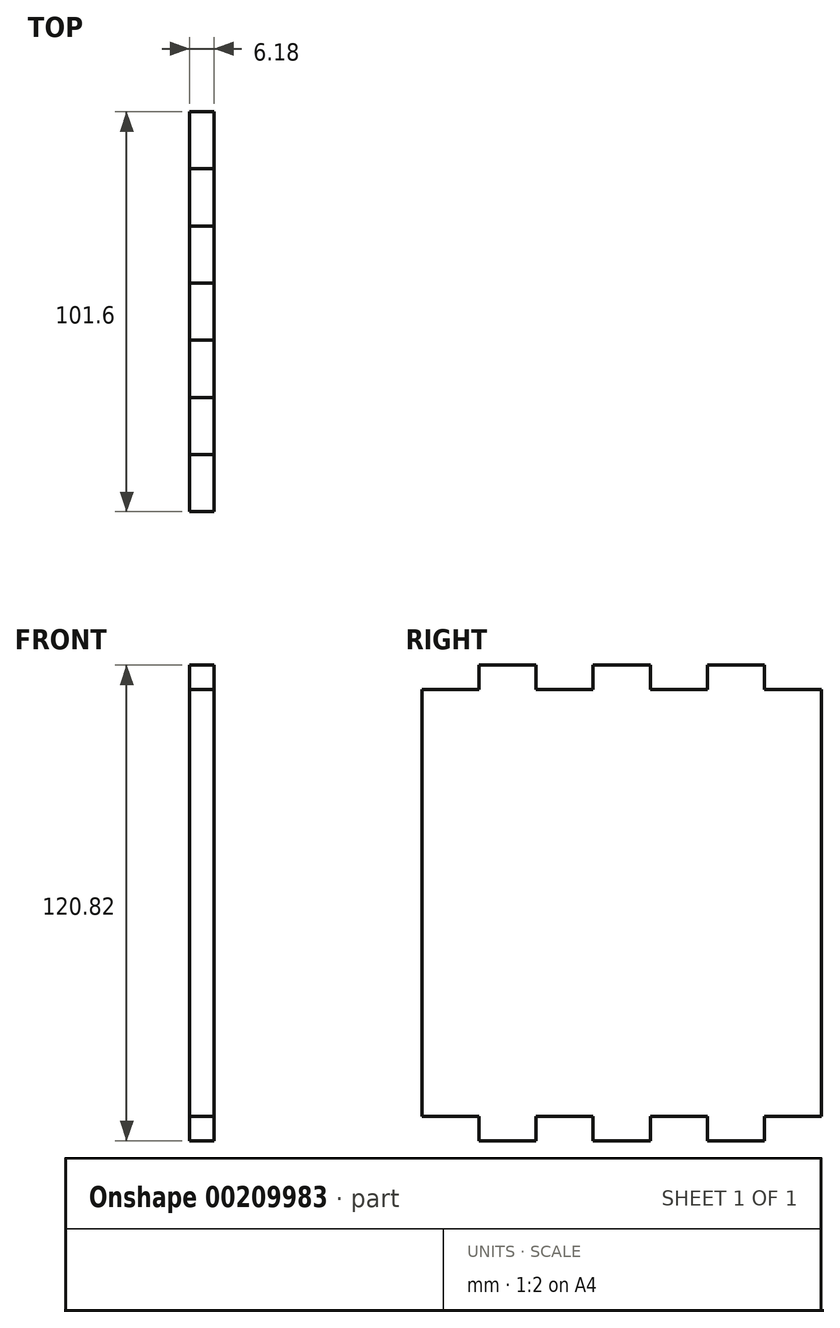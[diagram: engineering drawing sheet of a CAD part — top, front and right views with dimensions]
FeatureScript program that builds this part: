
annotation { "Feature Type Name" : "Feature", "Feature Type Description" : "" }
export const myFeature = defineFeature(function(context is Context, id is Id, definition is map)
    precondition{}
    {
        {
            var Q0;
            Q0=qCreatedBy(makeId("Right.planeOp"),FACE);
            var sketch = newSketch(context, id + "F0", { "sketchPlane" : qUnion([Q0])});
            skLineSegment(sketch, "E0.left", {"start": v(50.8, 54.22) * mm, "end": v(50.8, -54.22) * mm});
            skLineSegment(sketch, "E0.right", {"start": v(-50.8, 54.22) * mm, "end": v(-50.8, -54.22) * mm});
            skPoint(sketch, "E0.middle", {"position": v(0, 0) * mm});
            skLineSegment(sketch, "E1", {"start": v(-36.29, 60.4) * mm, "end": v(-36.29, 54.22) * mm});
            skLineSegment(sketch, "E2", {"start": v(-21.77, 54.22) * mm, "end": v(-21.77, 60.4) * mm});
            skLineSegment(sketch, "E3", {"start": v(7.25, 60.4) * mm, "end": v(7.25, 54.22) * mm});
            skLineSegment(sketch, "E4", {"start": v(7.25, 54.22) * mm, "end": v(7.25, 60.4) * mm});
            skLineSegment(sketch, "E5.MirrorCS", {"start": v(-7.25, 54.22) * mm, "end": v(-7.25, 60.4) * mm});
            skLineSegment(sketch, "E6.MirrorCS", {"start": v(-7.25, 60.4) * mm, "end": v(-7.25, 54.22) * mm});
            skLineSegment(sketch, "E7.MirrorCS", {"start": v(36.29, 60.4) * mm, "end": v(36.29, 54.22) * mm});
            skLineSegment(sketch, "E8.MirrorCS", {"start": v(21.77, 54.22) * mm, "end": v(21.77, 60.4) * mm});
            skLineSegment(sketch, "E9.MirrorCS", {"start": v(-7.25, -60.4) * mm, "end": v(-7.25, -54.22) * mm});
            skLineSegment(sketch, "E10.MirrorCS", {"start": v(-7.25, -54.22) * mm, "end": v(-7.25, -60.4) * mm});
            skLineSegment(sketch, "E11.MirrorCS", {"start": v(7.25, -54.22) * mm, "end": v(7.25, -60.4) * mm});
            skLineSegment(sketch, "E12.MirrorCS", {"start": v(7.25, -60.4) * mm, "end": v(7.25, -54.22) * mm});
            skLineSegment(sketch, "E13.MirrorCS", {"start": v(-21.77, -54.22) * mm, "end": v(-21.77, -60.4) * mm});
            skLineSegment(sketch, "E14.MirrorCS", {"start": v(-36.29, -60.4) * mm, "end": v(-36.29, -54.22) * mm});
            skLineSegment(sketch, "E15.MirrorCS", {"start": v(21.77, -54.22) * mm, "end": v(21.77, -60.4) * mm});
            skLineSegment(sketch, "E16.MirrorCS", {"start": v(36.29, -60.4) * mm, "end": v(36.29, -54.22) * mm});
            skLineSegment(sketch, "E17.MirrorCS", {"start": v(7.25, -60.4) * mm, "end": v(-7.25, -60.4) * mm});
            skLineSegment(sketch, "E18", {"start": v(36.29, 60.4) * mm, "end": v(21.77, 60.4) * mm});
            skLineSegment(sketch, "E19", {"start": v(-7.25, 60.4) * mm, "end": v(-7.25, 60.4) * mm});
            skLineSegment(sketch, "E20", {"start": v(-36.29, 54.22) * mm, "end": v(-50.8, 54.22) * mm});
            skLineSegment(sketch, "E21", {"start": v(-21.77, 54.22) * mm, "end": v(-7.25, 54.22) * mm});
            skLineSegment(sketch, "E22", {"start": v(7.25, 54.22) * mm, "end": v(21.77, 54.22) * mm});
            skLineSegment(sketch, "E23", {"start": v(36.29, 54.22) * mm, "end": v(50.8, 54.22) * mm});
            skLineSegment(sketch, "E24", {"start": v(36.29, -54.22) * mm, "end": v(50.8, -54.22) * mm});
            skLineSegment(sketch, "E25", {"start": v(21.77, -54.22) * mm, "end": v(7.25, -54.22) * mm});
            skLineSegment(sketch, "E26", {"start": v(-7.25, -54.22) * mm, "end": v(-21.77, -54.22) * mm});
            skLineSegment(sketch, "E27", {"start": v(-36.29, -54.22) * mm, "end": v(-50.8, -54.22) * mm});
            skLineSegment(sketch, "E28", {"start": v(36.29, -60.4) * mm, "end": v(21.77, -60.4) * mm});
            skLineSegment(sketch, "E29", {"start": v(-7.25, -60.4) * mm, "end": v(-7.25, -60.4) * mm});
            skLineSegment(sketch, "E30", {"start": v(-21.77, -60.4) * mm, "end": v(-36.29, -60.4) * mm});
            skPoint(sketch, "E31.orphan", {"position": v(50.8, -60.4) * mm});
            skPoint(sketch, "E32.MirrorCS.start.orphan", {"position": v(-50.8, -60.4) * mm});
            skLineSegment(sketch, "E33", {"start": v(-21.77, 60.4) * mm, "end": v(-36.29, 60.4) * mm});
            skPoint(sketch, "E34.MirrorCS.start.orphan", {"position": v(-50.8, 60.4) * mm});
            skPoint(sketch, "E35.orphan", {"position": v(50.8, 60.4) * mm});
            skLineSegment(sketch, "E36", {"start": v(7.25, 60.4) * mm, "end": v(-7.25, 60.4) * mm});
            skSolve(sketch);
        }
        {
            var Q0;
            Q0=makeQuery(id+"F0.imprint","IMPRINT",FACE,{"disambiguationData":[TD([[makeQuery(id+"F0.imprint","IMPRINT",EDGE,{"derivedFrom":sQuery(id+"F0.wireOp",EDGE,"E0.right")}),1.0]])]});
            extrude(context, id + "F1", {"entities" : qUnion([Q0]), "depth" : 6.18 * mm});
        }
    });
